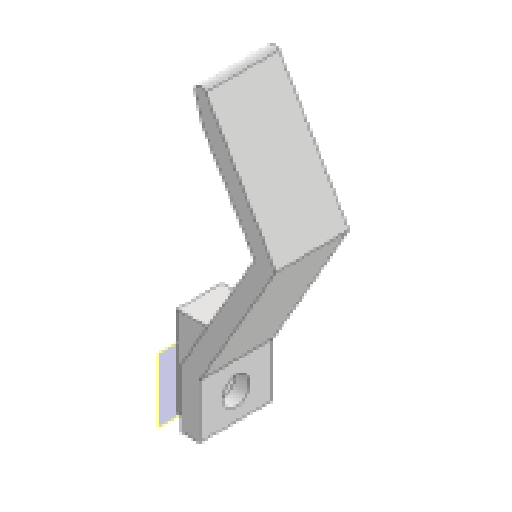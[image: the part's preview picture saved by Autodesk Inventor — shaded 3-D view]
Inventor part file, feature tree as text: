
AUTODESK INVENTOR PART (.ipt)
format: ipt  version: 2025 (Build 290162010, 162A)  size: 128,512 bytes
history: native  units: in
note: dims shown in document units (in); Inventor stores cm internally (conversion verified against a paired STEP export)
features: extrude x4, sketch x4, fillet x1, plane x1
ambient origin geometry x8: Origin, YZ Plane, XZ Plane, XY Plane, X Axis, Y Axis, Z Axis, Center Point
bodies: Solid1 (feature_tree)
feature tree (10):
  extrude  "Extrusion1"  Depth=0.2in
  fillet  "Fillet1"  Radius=0.8in
  plane  "Work Plane1"
  extrude  "Extrusion2"  Depth=0.2in
  extrude  "Extrusion3"  TaperAngle=120.0deg  [1 undecoded]
  extrude  "Extrusion4"  Depth=0.158in
  sketch  "Sketch1"  dims[d0=0.638in d1=0.2in d4=0.8in d5=0.0in]
  sketch  "Sketch2"  dims[d6=0.2in d7=0.2in]
  sketch  "Sketch3"  dims[d8=30.0deg d10=120.0deg]
  sketch  "Sketch4"  dims[d11=2.0in d12=1.525in d13=15.0deg d14=0.0625in d15=0.2in d16=0.49in d17=0.984in d18=0.245in d19=0.8in d20=0.0in d21=0.625in d22=0.0in d23=0.14in d24=0.3in d25=0.158in d26=0.0in]
note: 1 required parameter value undecoded (feature->parameter linkage not recoverable at this tier; creation-order binding heuristic only, values carry confidence <= 0.55)
